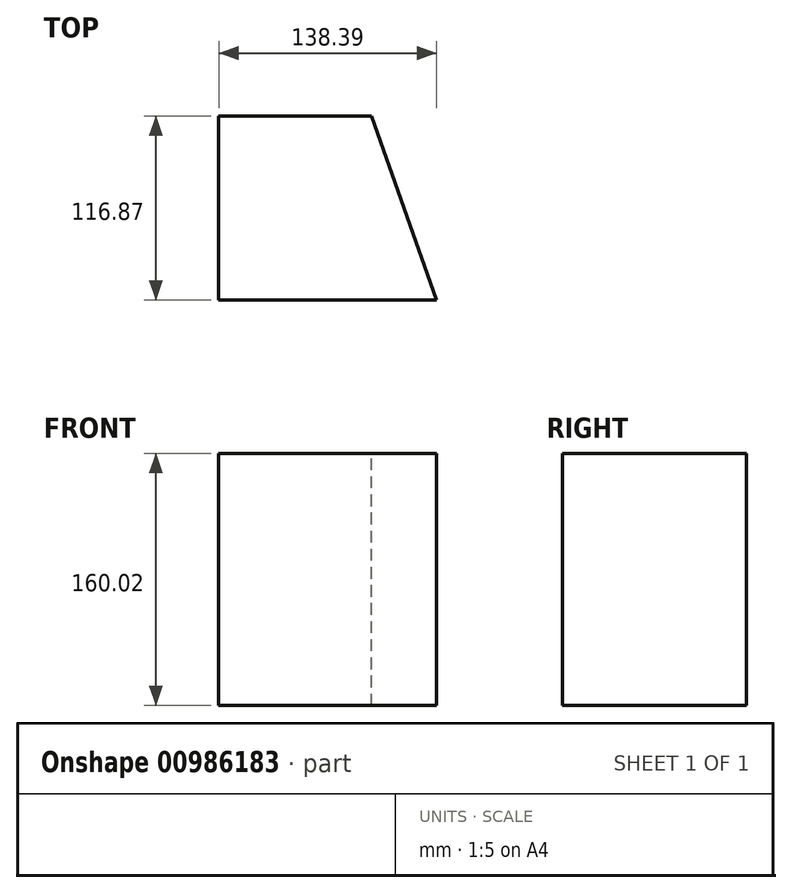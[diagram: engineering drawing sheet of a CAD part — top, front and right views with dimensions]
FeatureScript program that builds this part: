
annotation { "Feature Type Name" : "Feature", "Feature Type Description" : "" }
export const myFeature = defineFeature(function(context is Context, id is Id, definition is map)
    precondition{}
    {
        {
            var Q0;
            Q0=qCreatedBy(makeId("Top.planeOp"),FACE);
            var sketch = newSketch(context, id + "F0", { "sketchPlane" : qUnion([Q0])});
            skLineSegment(sketch, "E0", {"start": v(-75.83, -93.1) * mm, "end": v(-214.22, -93.1) * mm});
            skLineSegment(sketch, "E1", {"start": v(-214.22, -93.1) * mm, "end": v(-214.22, 23.76) * mm});
            skLineSegment(sketch, "E2", {"start": v(-214.22, 23.76) * mm, "end": v(-117.18, 23.76) * mm});
            skLineSegment(sketch, "E3", {"start": v(-117.18, 23.76) * mm, "end": v(-75.83, -93.1) * mm});
            skSolve(sketch);
        }
        {
            var Q0;
            Q0=makeQuery(id+"F0.imprint","IMPRINT",FACE,{"disambiguationData":[TD([[makeQuery(id+"F0.imprint","IMPRINT",EDGE,{"derivedFrom":sQuery(id+"F0.wireOp",EDGE,"E0")}),-1.0]])]});
            extrude(context, id + "F1", {"entities" : qUnion([Q0]), "oppositeDirection" : true, "depth" : 160.02 * mm, "offsetDistance" : 25.4 * mm});
        }
    });
